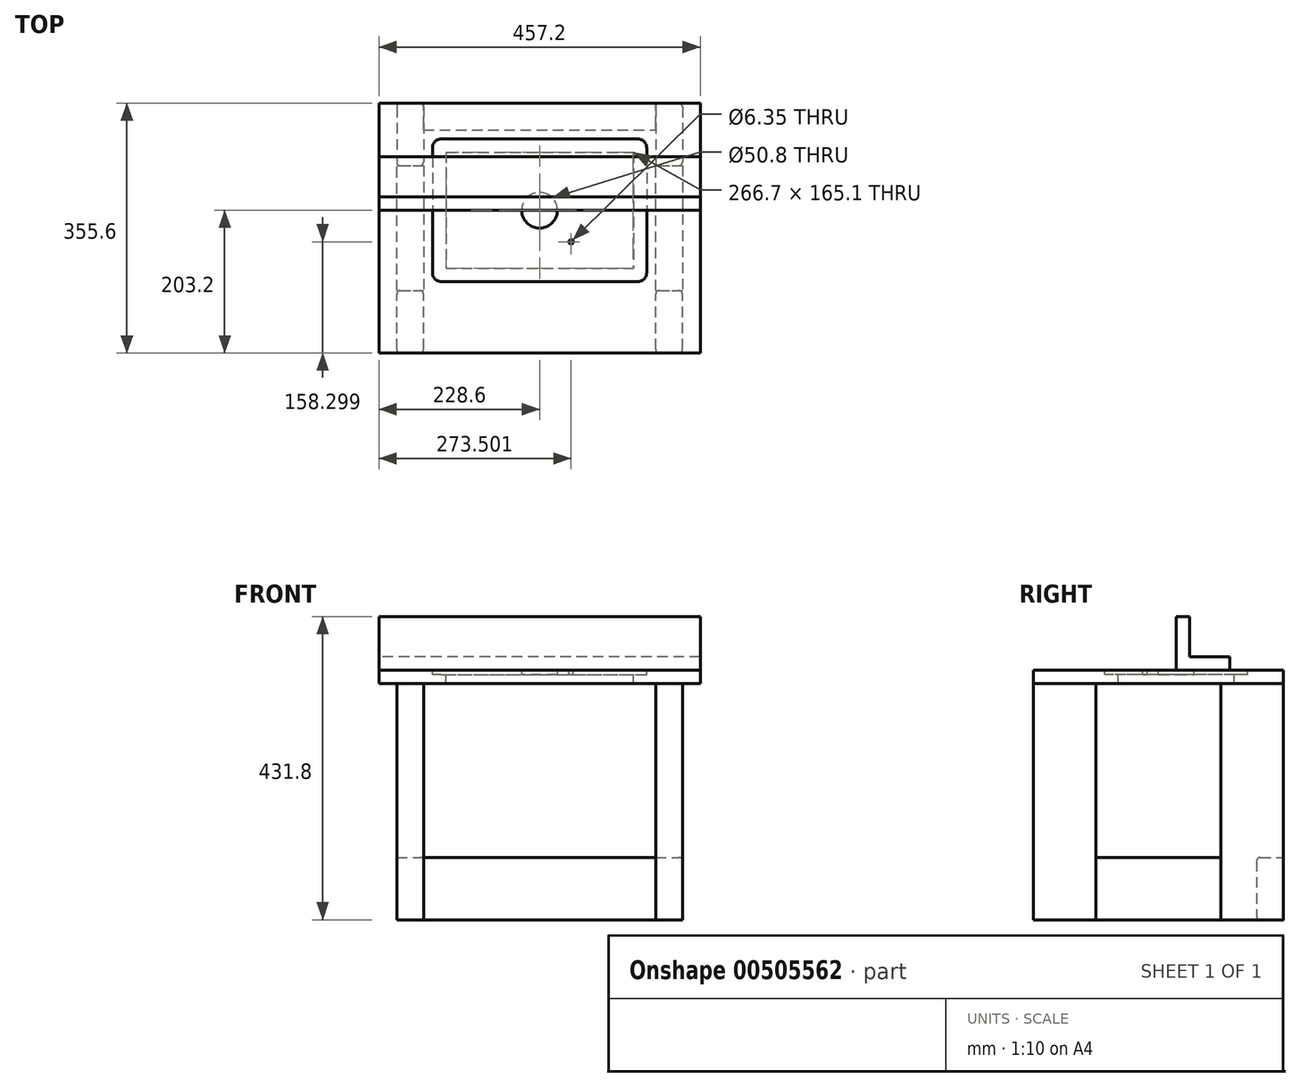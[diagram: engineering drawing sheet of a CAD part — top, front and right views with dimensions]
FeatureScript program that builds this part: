
annotation { "Feature Type Name" : "Feature", "Feature Type Description" : "" }
export const myFeature = defineFeature(function(context is Context, id is Id, definition is map)
    precondition{}
    {
        {
            var Q0;
            Q0=qCreatedBy(makeId("Top.planeOp"),FACE);
            var sketch = newSketch(context, id + "F0", { "sketchPlane" : qUnion([Q0])});
            skLineSegment(sketch, "E0.bottom", {"start": v(228.6, -177.8) * mm, "end": v(-228.6, -177.8) * mm});
            skLineSegment(sketch, "E0.top", {"start": v(228.6, 177.8) * mm, "end": v(-228.6, 177.8) * mm});
            skLineSegment(sketch, "E0.left", {"start": v(228.6, -177.8) * mm, "end": v(228.6, 177.8) * mm});
            skLineSegment(sketch, "E0.right", {"start": v(-228.6, -177.8) * mm, "end": v(-228.6, 177.8) * mm});
            skPoint(sketch, "E0.middle", {"position": v(0, 0) * mm});
            skLineSegment(sketch, "E1.bottom", {"start": v(-152.4, 127) * mm, "end": v(152.4, 127) * mm});
            skLineSegment(sketch, "E1.top", {"start": v(-152.4, -76.2) * mm, "end": v(152.4, -76.2) * mm});
            skLineSegment(sketch, "E1.left", {"start": v(-152.4, 127) * mm, "end": v(-152.4, -76.2) * mm});
            skLineSegment(sketch, "E1.right", {"start": v(152.4, 127) * mm, "end": v(152.4, -76.2) * mm});
            skLineSegment(sketch, "E2", {"start": v(0, 177.8) * mm, "end": v(0, -177.8) * mm, "construction": true});
            skLineSegment(sketch, "E3.0", {"start": v(-133.35, 107.95) * mm, "end": v(-133.35, -57.15) * mm});
            skLineSegment(sketch, "E3.1", {"start": v(-133.35, 107.95) * mm, "end": v(133.35, 107.95) * mm});
            skLineSegment(sketch, "E3.2", {"start": v(133.35, 107.95) * mm, "end": v(133.35, -57.15) * mm});
            skLineSegment(sketch, "E3.3", {"start": v(-133.35, -57.15) * mm, "end": v(133.35, -57.15) * mm});
            skSolve(sketch);
        }
        {
            var Q0;
            Q0=makeQuery(id+"F0.imprint","IMPRINT",FACE,{"disambiguationData":[TD([[makeQuery(id+"F0.imprint","IMPRINT",EDGE,{"derivedFrom":sQuery(id+"F0.wireOp",EDGE,"E0.bottom")}),-1.0]])]});
            var Q1;
            Q1=makeQuery(id+"F0.imprint","IMPRINT",FACE,{"disambiguationData":[TD([[makeQuery(id+"F0.imprint","IMPRINT",EDGE,{"derivedFrom":sQuery(id+"F0.wireOp",EDGE,"E1.bottom")}),-1.0]])]});
            extrude(context, id + "F1", {"entities" : qUnion([Q0, Q1]), "oppositeDirection" : true, "depth" : 19.05 * mm});
        }
        {
            var Q0;
            Q0=makeQuery(id+"F0.imprint","IMPRINT",FACE,{"disambiguationData":[TD([[makeQuery(id+"F0.imprint","IMPRINT",EDGE,{"derivedFrom":sQuery(id+"F0.wireOp",EDGE,"E1.bottom")}),-1.0]])]});
            extrude(context, id + "F2", {"entities" : qUnion([Q0]), "operationType" : NewBodyOperationType.REMOVE, "oppositeDirection" : true, "depth" : 6.35 * mm});
        }
        {
            var Q0;
            Q0=makeQuery(id+"F1.opExtrude","SWEPT_BODY",BODY,{"disambiguationData":[OSD([sQuery(id+"F0.wireOp",EDGE,"E0.bottom"),sQuery(id+"F0.wireOp",EDGE,"E0.top"),sQuery(id+"F0.wireOp",EDGE,"E0.left"),sQuery(id+"F0.wireOp",EDGE,"E0.right"),sQuery(id+"F0.wireOp",EDGE,"E3.0"),sQuery(id+"F0.wireOp",EDGE,"E3.1"),sQuery(id+"F0.wireOp",EDGE,"E3.2"),sQuery(id+"F0.wireOp",EDGE,"E3.3")])]});
            transform(context, id + "F3", {"entities" : qUnion([Q0]), "transformType" : TransformType.TRANSLATION_3D, "dx" : 0 * mm, "dy" : 0 * mm, "dz" : 355.6 * mm, "makeCopy" : false});
        }
        {
            var Q0;
            Q0=makeQuery(id+"F1.opExtrude","SWEPT_FACE",FACE,{"disambiguationData":[OSD([sQuery(id+"F0.wireOp",EDGE,"E0.left")])]});
            var sketch = newSketch(context, id + "F4", { "sketchPlane" : qUnion([Q0])});
            skLineSegment(sketch, "E4.bottom", {"start": v(-177.8, 336.55) * mm, "end": v(-88.9, 336.55) * mm});
            skLineSegment(sketch, "E4.top", {"start": v(-177.8, 0) * mm, "end": v(-88.9, 0) * mm});
            skLineSegment(sketch, "E4.left", {"start": v(-177.8, 336.55) * mm, "end": v(-177.8, 0) * mm});
            skLineSegment(sketch, "E4.right", {"start": v(-88.9, 336.55) * mm, "end": v(-88.9, 0) * mm});
            skLineSegment(sketch, "E5.bottom", {"start": v(177.8, 336.55) * mm, "end": v(88.9, 336.55) * mm});
            skLineSegment(sketch, "E5.top", {"start": v(177.8, 0) * mm, "end": v(88.9, 0) * mm});
            skLineSegment(sketch, "E5.left", {"start": v(177.8, 336.55) * mm, "end": v(177.8, 0) * mm});
            skLineSegment(sketch, "E5.right", {"start": v(88.9, 336.55) * mm, "end": v(88.9, 0) * mm});
            skLineSegment(sketch, "E6.bottom", {"start": v(88.9, 0) * mm, "end": v(-88.9, 0) * mm});
            skLineSegment(sketch, "E6.top", {"start": v(88.9, 88.9) * mm, "end": v(-88.9, 88.9) * mm});
            skLineSegment(sketch, "E6.left", {"start": v(88.9, 0) * mm, "end": v(88.9, 88.9) * mm});
            skLineSegment(sketch, "E6.right", {"start": v(-88.9, 0) * mm, "end": v(-88.9, 88.9) * mm});
            skSolve(sketch);
        }
        {
            var Q0;
            Q0=makeQuery(id+"F4.imprint","IMPRINT",FACE,{"disambiguationData":[TD([[makeQuery(id+"F4.imprint","IMPRINT",EDGE,{"derivedFrom":sQuery(id+"F4.wireOp",EDGE,"E4.bottom")}),-1.0]])]});
            var Q1;
            Q1=makeQuery(id+"F4.imprint","IMPRINT",FACE,{"disambiguationData":[TD([[makeQuery(id+"F4.imprint","IMPRINT",EDGE,{"derivedFrom":sQuery(id+"F4.wireOp",EDGE,"E5.bottom")}),-1.0]])]});
            extrude(context, id + "F5", {"entities" : qUnion([Q0, Q1]), "oppositeDirection" : true, "depth" : 38.1 * mm});
        }
        {
            var Q0;
            Q0=makeQuery(id+"F4.imprint","IMPRINT",FACE,{"disambiguationData":[TD([[makeQuery(id+"F4.imprint","IMPRINT",EDGE,{"derivedFrom":sQuery(id+"F4.wireOp",EDGE,"E6.bottom")}),-1.0]])]});
            var Q1;
            Q1=makeQuery(id+"F5.opExtrude","CAP_FACE",FACE,{"disambiguationData":[OSD([sQuery(id+"F4.wireOp",EDGE,"E4.bottom"),sQuery(id+"F4.wireOp",EDGE,"E4.top"),sQuery(id+"F4.wireOp",EDGE,"E4.left"),sQuery(id+"F4.wireOp",EDGE,"E4.right"),sQuery(id+"F4.wireOp",EDGE,"E6.right")])],"isStart":false});
            extrude(context, id + "F6", {"entities" : qUnion([Q0]), "endBound" : BoundingType.UP_TO_SURFACE, "oppositeDirection" : true, "endBoundEntityFace" : qUnion([Q1]), "depth" : 25.4 * mm});
        }
        {
            var Q0;
            Q0=makeQuery(id+"F5.opExtrude","SWEPT_BODY",BODY,{"disambiguationData":[OSD([sQuery(id+"F4.wireOp",EDGE,"E4.bottom"),sQuery(id+"F4.wireOp",EDGE,"E4.top"),sQuery(id+"F4.wireOp",EDGE,"E4.left"),sQuery(id+"F4.wireOp",EDGE,"E4.right"),sQuery(id+"F4.wireOp",EDGE,"E6.right")])]});
            var Q1;
            Q1=makeQuery(id+"F5.opExtrude","SWEPT_BODY",BODY,{"disambiguationData":[OSD([sQuery(id+"F4.wireOp",EDGE,"E5.bottom"),sQuery(id+"F4.wireOp",EDGE,"E5.top"),sQuery(id+"F4.wireOp",EDGE,"E5.left"),sQuery(id+"F4.wireOp",EDGE,"E5.right"),sQuery(id+"F4.wireOp",EDGE,"E6.left")])]});
            var Q2;
            Q2=makeQuery(id+"F6.opExtrude","SWEPT_BODY",BODY,{"disambiguationData":[OSD([sQuery(id+"F4.wireOp",EDGE,"E6.bottom"),sQuery(id+"F4.wireOp",EDGE,"E6.top"),sQuery(id+"F4.wireOp",EDGE,"E6.left"),sQuery(id+"F4.wireOp",EDGE,"E6.right")])]});
            var Q3;
            Q3=makeQuery(id+"F1.opExtrude","CAP_EDGE",EDGE,{"disambiguationData":[OSD([sQuery(id+"F0.wireOp",EDGE,"E0.bottom")])],"isStart":false});
            var Q4;
            Q4=makeQuery(id+"F1.opExtrude","CAP_EDGE",EDGE,{"disambiguationData":[OSD([sQuery(id+"F0.wireOp",EDGE,"E0.bottom")])],"isStart":false});
            transform(context, id + "F7", {"entities" : qUnion([Q0, Q1, Q2]), "transformType" : TransformType.TRANSLATION_DISTANCE, "transformDirection" : qUnion([Q4]), "distance" : 393.7 * mm, "makeCopy" : true});
        }
        {
            var Q0;
            Q0=makeQuery(id+"F5.opExtrude","SWEPT_BODY",BODY,{"disambiguationData":[OSD([sQuery(id+"F4.wireOp",EDGE,"E5.bottom"),sQuery(id+"F4.wireOp",EDGE,"E5.top"),sQuery(id+"F4.wireOp",EDGE,"E5.left"),sQuery(id+"F4.wireOp",EDGE,"E5.right"),sQuery(id+"F4.wireOp",EDGE,"E6.left")])]});
            var Q1;
            Q1=makeQuery(id+"F5.opExtrude","SWEPT_BODY",BODY,{"disambiguationData":[OSD([sQuery(id+"F4.wireOp",EDGE,"E4.bottom"),sQuery(id+"F4.wireOp",EDGE,"E4.top"),sQuery(id+"F4.wireOp",EDGE,"E4.left"),sQuery(id+"F4.wireOp",EDGE,"E4.right"),sQuery(id+"F4.wireOp",EDGE,"E6.right")])]});
            var Q2;
            Q2=makeQuery(id+"F6.opExtrude","SWEPT_BODY",BODY,{"disambiguationData":[OSD([sQuery(id+"F4.wireOp",EDGE,"E6.bottom"),sQuery(id+"F4.wireOp",EDGE,"E6.top"),sQuery(id+"F4.wireOp",EDGE,"E6.left"),sQuery(id+"F4.wireOp",EDGE,"E6.right")])]});
            var Q3;
            Q3=makeQuery(id+"F1.opExtrude","CAP_EDGE",EDGE,{"disambiguationData":[OSD([sQuery(id+"F0.wireOp",EDGE,"E0.bottom")])],"isStart":false});
            transform(context, id + "F8", {"entities" : qUnion([Q0, Q1, Q2]), "transformType" : TransformType.TRANSLATION_DISTANCE, "transformDirection" : qUnion([Q3]), "distance" : 25.4 * mm, "makeCopy" : false});
        }
        {
            var Q0;
            Q0=makeQuery(id+"F1.opExtrude","SWEPT_FACE",FACE,{"disambiguationData":[OSD([sQuery(id+"F0.wireOp",EDGE,"E0.top")])]});
            var sketch = newSketch(context, id + "F9", { "sketchPlane" : qUnion([Q0])});
            skLineSegment(sketch, "E7.0", {"start": v(165.1, 336.55) * mm, "end": v(165.1, 0) * mm});
            skLineSegment(sketch, "E8.0", {"start": v(-165.1, 336.55) * mm, "end": v(-165.1, 0) * mm});
            skLineSegment(sketch, "E9.bottom", {"start": v(165.1, 0) * mm, "end": v(-165.1, 0) * mm});
            skLineSegment(sketch, "E9.top", {"start": v(165.1, 88.9) * mm, "end": v(-165.1, 88.9) * mm});
            skLineSegment(sketch, "E9.left", {"start": v(165.1, 0) * mm, "end": v(165.1, 88.9) * mm});
            skLineSegment(sketch, "E9.right", {"start": v(-165.1, 0) * mm, "end": v(-165.1, 88.9) * mm});
            skSolve(sketch);
        }
        {
            var Q0;
            Q0=makeQuery(id+"F9.imprint","IMPRINT",FACE,{"disambiguationData":[TD([[makeQuery(id+"F9.imprint","IMPRINT",EDGE,{"derivedFrom":sQuery(id+"F9.wireOp",EDGE,"E9.bottom")}),-1.0]])]});
            extrude(context, id + "F10", {"entities" : qUnion([Q0]), "oppositeDirection" : true, "depth" : 38.1 * mm, "offsetDistance" : 25.4 * mm});
        }
        {
            var Q0;
            Q0=makeQuery(id+"F5.opExtrude","CAP_EDGE",EDGE,{"disambiguationData":[OSD([sQuery(id+"F4.wireOp",EDGE,"E4.left")])],"isStart":true});
            var Q1;
            Q1=makeQuery(id+"F5.opExtrude","CAP_EDGE",EDGE,{"disambiguationData":[OSD([sQuery(id+"F4.wireOp",EDGE,"E4.left")])],"isStart":false});
            var Q2;
            Q2=makeQuery(id+"F5.opExtrude","CAP_EDGE",EDGE,{"disambiguationData":[OSD([sQuery(id+"F4.wireOp",EDGE,"E4.right"),sQuery(id+"F4.wireOp",EDGE,"E6.right")])],"isStart":true});
            var Q3;
            Q3=makeQuery(id+"F6.opExtrude","TWEAK_EDGE",EDGE,{"derivedFrom":[makeQuery(id+"F4.imprint","IMPRINT",EDGE,{"derivedFrom":sQuery(id+"F4.wireOp",EDGE,"E6.top")}),makeQuery(id+"F5.opExtrude","CAP_FACE",FACE,{"disambiguationData":[OSD([sQuery(id+"F4.wireOp",EDGE,"E4.bottom"),sQuery(id+"F4.wireOp",EDGE,"E4.top"),sQuery(id+"F4.wireOp",EDGE,"E4.left"),sQuery(id+"F4.wireOp",EDGE,"E4.right"),sQuery(id+"F4.wireOp",EDGE,"E6.right")])],"isStart":false})]});
            var Q4;
            Q4=makeQuery(id+"F6.opExtrude","CAP_EDGE",EDGE,{"disambiguationData":[OSD([sQuery(id+"F4.wireOp",EDGE,"E6.top")])],"isStart":true});
            var Q5;
            Q5=makeQuery(id+"F6.opExtrude","CAP_EDGE",EDGE,{"disambiguationData":[OSD([sQuery(id+"F4.wireOp",EDGE,"E6.bottom")])],"isStart":true});
            var Q6;
            Q6=makeQuery(id+"F5.opExtrude","CAP_EDGE",EDGE,{"disambiguationData":[OSD([sQuery(id+"F4.wireOp",EDGE,"E5.right"),sQuery(id+"F4.wireOp",EDGE,"E6.left")])],"isStart":true});
            var Q7;
            Q7=makeQuery(id+"F5.opExtrude","CAP_EDGE",EDGE,{"disambiguationData":[OSD([sQuery(id+"F4.wireOp",EDGE,"E5.right"),sQuery(id+"F4.wireOp",EDGE,"E6.left")])],"isStart":false});
            var Q8;
            Q8=makeQuery(id+"F5.opExtrude","CAP_EDGE",EDGE,{"disambiguationData":[OSD([sQuery(id+"F4.wireOp",EDGE,"E5.left")])],"isStart":true});
            var Q9;
            Q9=makeQuery(id+"F5.opExtrude","CAP_EDGE",EDGE,{"disambiguationData":[OSD([sQuery(id+"F4.wireOp",EDGE,"E4.right"),sQuery(id+"F4.wireOp",EDGE,"E6.right")])],"isStart":false});
            var Q10;
            Q10=makeQuery(id+"F6.opExtrude","TWEAK_EDGE",EDGE,{"derivedFrom":[makeQuery(id+"F4.imprint","IMPRINT",EDGE,{"derivedFrom":sQuery(id+"F4.wireOp",EDGE,"E6.bottom")}),makeQuery(id+"F5.opExtrude","CAP_FACE",FACE,{"disambiguationData":[OSD([sQuery(id+"F4.wireOp",EDGE,"E4.bottom"),sQuery(id+"F4.wireOp",EDGE,"E4.top"),sQuery(id+"F4.wireOp",EDGE,"E4.left"),sQuery(id+"F4.wireOp",EDGE,"E4.right"),sQuery(id+"F4.wireOp",EDGE,"E6.right")])],"isStart":false})]});
            var Q11;
            Q11=makeQuery(id+"F5.opExtrude","CAP_EDGE",EDGE,{"disambiguationData":[OSD([sQuery(id+"F4.wireOp",EDGE,"E5.left")])],"isStart":false});
            var Q12;
            Q12=makeQuery(id+"F7.opPattern","COPY",EDGE,{"derivedFrom":makeQuery(id+"F6.opExtrude","TWEAK_EDGE",EDGE,{"derivedFrom":[makeQuery(id+"F4.imprint","IMPRINT",EDGE,{"derivedFrom":sQuery(id+"F4.wireOp",EDGE,"E6.top")}),makeQuery(id+"F5.opExtrude","CAP_FACE",FACE,{"disambiguationData":[OSD([sQuery(id+"F4.wireOp",EDGE,"E4.bottom"),sQuery(id+"F4.wireOp",EDGE,"E4.top"),sQuery(id+"F4.wireOp",EDGE,"E4.left"),sQuery(id+"F4.wireOp",EDGE,"E4.right"),sQuery(id+"F4.wireOp",EDGE,"E6.right")])],"isStart":false})]}),"instanceName":"1"});
            var Q13;
            Q13=makeQuery(id+"F7.opPattern","COPY",EDGE,{"derivedFrom":makeQuery(id+"F6.opExtrude","CAP_EDGE",EDGE,{"disambiguationData":[OSD([sQuery(id+"F4.wireOp",EDGE,"E6.top")])],"isStart":true}),"instanceName":"1"});
            var Q14;
            Q14=makeQuery(id+"F7.opPattern","COPY",EDGE,{"derivedFrom":makeQuery(id+"F6.opExtrude","CAP_EDGE",EDGE,{"disambiguationData":[OSD([sQuery(id+"F4.wireOp",EDGE,"E6.bottom")])],"isStart":true}),"instanceName":"1"});
            var Q15;
            Q15=makeQuery(id+"F7.opPattern","COPY",EDGE,{"derivedFrom":makeQuery(id+"F5.opExtrude","CAP_EDGE",EDGE,{"disambiguationData":[OSD([sQuery(id+"F4.wireOp",EDGE,"E4.right"),sQuery(id+"F4.wireOp",EDGE,"E6.right")])],"isStart":true}),"instanceName":"1"});
            var Q16;
            Q16=makeQuery(id+"F7.opPattern","COPY",EDGE,{"derivedFrom":makeQuery(id+"F5.opExtrude","CAP_EDGE",EDGE,{"disambiguationData":[OSD([sQuery(id+"F4.wireOp",EDGE,"E4.left")])],"isStart":true}),"instanceName":"1"});
            var Q17;
            Q17=makeQuery(id+"F7.opPattern","COPY",EDGE,{"derivedFrom":makeQuery(id+"F5.opExtrude","CAP_EDGE",EDGE,{"disambiguationData":[OSD([sQuery(id+"F4.wireOp",EDGE,"E4.left")])],"isStart":false}),"instanceName":"1"});
            var Q18;
            Q18=makeQuery(id+"F7.opPattern","COPY",EDGE,{"derivedFrom":makeQuery(id+"F5.opExtrude","CAP_EDGE",EDGE,{"disambiguationData":[OSD([sQuery(id+"F4.wireOp",EDGE,"E5.right"),sQuery(id+"F4.wireOp",EDGE,"E6.left")])],"isStart":false}),"instanceName":"1"});
            var Q19;
            Q19=makeQuery(id+"F7.opPattern","COPY",EDGE,{"derivedFrom":makeQuery(id+"F5.opExtrude","CAP_EDGE",EDGE,{"disambiguationData":[OSD([sQuery(id+"F4.wireOp",EDGE,"E5.right"),sQuery(id+"F4.wireOp",EDGE,"E6.left")])],"isStart":true}),"instanceName":"1"});
            var Q20;
            Q20=makeQuery(id+"F7.opPattern","COPY",EDGE,{"derivedFrom":makeQuery(id+"F5.opExtrude","CAP_EDGE",EDGE,{"disambiguationData":[OSD([sQuery(id+"F4.wireOp",EDGE,"E5.left")])],"isStart":true}),"instanceName":"1"});
            var Q21;
            Q21=makeQuery(id+"F7.opPattern","COPY",EDGE,{"derivedFrom":makeQuery(id+"F5.opExtrude","CAP_EDGE",EDGE,{"disambiguationData":[OSD([sQuery(id+"F4.wireOp",EDGE,"E4.right"),sQuery(id+"F4.wireOp",EDGE,"E6.right")])],"isStart":false}),"instanceName":"1"});
            var Q22;
            Q22=makeQuery(id+"F7.opPattern","COPY",EDGE,{"derivedFrom":makeQuery(id+"F6.opExtrude","TWEAK_EDGE",EDGE,{"derivedFrom":[makeQuery(id+"F4.imprint","IMPRINT",EDGE,{"derivedFrom":sQuery(id+"F4.wireOp",EDGE,"E6.bottom")}),makeQuery(id+"F5.opExtrude","CAP_FACE",FACE,{"disambiguationData":[OSD([sQuery(id+"F4.wireOp",EDGE,"E4.bottom"),sQuery(id+"F4.wireOp",EDGE,"E4.top"),sQuery(id+"F4.wireOp",EDGE,"E4.left"),sQuery(id+"F4.wireOp",EDGE,"E4.right"),sQuery(id+"F4.wireOp",EDGE,"E6.right")])],"isStart":false})]}),"instanceName":"1"});
            var Q23;
            Q23=makeQuery(id+"F7.opPattern","COPY",EDGE,{"derivedFrom":makeQuery(id+"F5.opExtrude","CAP_EDGE",EDGE,{"disambiguationData":[OSD([sQuery(id+"F4.wireOp",EDGE,"E5.left")])],"isStart":false}),"instanceName":"1"});
            var Q24;
            Q24=makeQuery(id+"F10.opExtrude","CAP_EDGE",EDGE,{"disambiguationData":[OSD([sQuery(id+"F9.wireOp",EDGE,"E9.top")])],"isStart":false});
            var Q25;
            Q25=makeQuery(id+"F10.opExtrude","CAP_EDGE",EDGE,{"disambiguationData":[OSD([sQuery(id+"F9.wireOp",EDGE,"E9.bottom")])],"isStart":true});
            var Q26;
            Q26=makeQuery(id+"F10.opExtrude","CAP_EDGE",EDGE,{"disambiguationData":[OSD([sQuery(id+"F9.wireOp",EDGE,"E9.bottom")])],"isStart":false});
            fillet(context, id + "F11", {"entities" : qUnion([Q0, Q1, Q2, Q3, Q4, Q5, Q6, Q7, Q8, Q9, Q10, Q11, Q12, Q13, Q14, Q15, Q16, Q17, Q18, Q19, Q20, Q21, Q22, Q23, Q24, Q25, Q26]), "radius" : 5.08 * mm, "tangentPropagation" : true, "allowEdgeOverflow" : false});
        }
        {
            var Q0;
            Q0=makeQuery(id+"F2.boolean.opBoolean","COPY",EDGE,{"derivedFrom":makeQuery(id+"F2.opExtrude","SWEPT_EDGE",EDGE,{"disambiguationData":[OSD([sQuery(id+"F0.wireOp",EDGE,"E1.bottom"),sQuery(id+"F0.wireOp",EDGE,"E1.left")])]})});
            var Q1;
            Q1=makeQuery(id+"F2.boolean.opBoolean","COPY",EDGE,{"derivedFrom":makeQuery(id+"F2.opExtrude","SWEPT_EDGE",EDGE,{"disambiguationData":[OSD([sQuery(id+"F0.wireOp",EDGE,"E1.bottom"),sQuery(id+"F0.wireOp",EDGE,"E1.right")])]})});
            var Q2;
            Q2=makeQuery(id+"F2.boolean.opBoolean","COPY",EDGE,{"derivedFrom":makeQuery(id+"F2.opExtrude","SWEPT_EDGE",EDGE,{"disambiguationData":[OSD([sQuery(id+"F0.wireOp",EDGE,"E1.top"),sQuery(id+"F0.wireOp",EDGE,"E1.right")])]})});
            var Q3;
            Q3=makeQuery(id+"F2.boolean.opBoolean","COPY",EDGE,{"derivedFrom":makeQuery(id+"F2.opExtrude","SWEPT_EDGE",EDGE,{"disambiguationData":[OSD([sQuery(id+"F0.wireOp",EDGE,"E1.top"),sQuery(id+"F0.wireOp",EDGE,"E1.left")])]})});
            fillet(context, id + "F12", {"entities" : qUnion([Q0, Q1, Q2, Q3]), "radius" : 12.7 * mm, "tangentPropagation" : true, "allowEdgeOverflow" : false});
        }
        {
            var Q0;
            Q0=makeQuery(id+"F1.opExtrude","CAP_FACE",FACE,{"disambiguationData":[OSD([sQuery(id+"F0.wireOp",EDGE,"E0.bottom"),sQuery(id+"F0.wireOp",EDGE,"E0.top"),sQuery(id+"F0.wireOp",EDGE,"E0.left"),sQuery(id+"F0.wireOp",EDGE,"E0.right"),sQuery(id+"F0.wireOp",EDGE,"E3.0"),sQuery(id+"F0.wireOp",EDGE,"E3.1"),sQuery(id+"F0.wireOp",EDGE,"E3.2"),sQuery(id+"F0.wireOp",EDGE,"E3.3")])],"isStart":true});
            var sketch = newSketch(context, id + "F13", { "sketchPlane" : qUnion([Q0])});
            skLineSegment(sketch, "E10.0.0", {"start": v(139.7, 127) * mm, "end": v(-139.7, 127) * mm});
            skArc(sketch, "E10.0.1", {"start": v(-139.7, 127) * mm, "mid": v(-148.68, 123.28) * mm, "end": v(-152.4, 114.3) * mm});
            skLineSegment(sketch, "E10.0.2", {"start": v(-152.4, 114.3) * mm, "end": v(-152.4, -63.5) * mm});
            skArc(sketch, "E10.0.3", {"start": v(-152.4, -63.5) * mm, "mid": v(-148.68, -72.48) * mm, "end": v(-139.7, -76.2) * mm});
            skLineSegment(sketch, "E10.0.4", {"start": v(-139.7, -76.2) * mm, "end": v(139.7, -76.2) * mm});
            skArc(sketch, "E10.0.5", {"start": v(139.7, -76.2) * mm, "mid": v(148.68, -72.48) * mm, "end": v(152.4, -63.5) * mm});
            skLineSegment(sketch, "E10.0.6", {"start": v(152.4, -63.5) * mm, "end": v(152.4, 114.3) * mm});
            skArc(sketch, "E10.0.7", {"start": v(152.4, 114.3) * mm, "mid": v(148.68, 123.28) * mm, "end": v(139.7, 127) * mm});
            skLineSegment(sketch, "E11", {"start": v(0, 127) * mm, "end": v(0, -76.2) * mm, "construction": true});
            skLineSegment(sketch, "E12", {"start": v(152.4, 25.4) * mm, "end": v(-152.4, 25.4) * mm, "construction": true});
            skCircle(sketch, "E13", {"center": v(0, 25.4) * mm, "radius": 76.2 * mm, "construction": true});
            skCircle(sketch, "E14", {"center": v(0, 25.4) * mm, "radius": 25.4 * mm});
            skLineSegment(sketch, "E15", {"start": v(0, 25.4) * mm, "end": v(44.9, -19.5) * mm, "construction": true});
            skCircle(sketch, "E16", {"center": v(44.9, -19.5) * mm, "radius": 3.18 * mm});
            skSolve(sketch);
        }
        {
            var Q0;
            Q0 = qSketchRegion(id + "F13", true);
            extrude(context, id + "F14", {"entities" : qUnion([Q0]), "oppositeDirection" : true, "depth" : 6.35 * mm});
        }
        {
            var Q0;
            Q0=qCreatedBy(makeId("Right.planeOp"),FACE);
            var sketch = newSketch(context, id + "F15", { "sketchPlane" : qUnion([Q0])});
            skLineSegment(sketch, "E17.bottom", {"start": v(25.4, 431.8) * mm, "end": v(101.6, 431.8) * mm, "construction": true});
            skLineSegment(sketch, "E17.top", {"start": v(25.4, 355.6) * mm, "end": v(101.6, 355.6) * mm});
            skLineSegment(sketch, "E17.left", {"start": v(25.4, 431.8) * mm, "end": v(25.4, 355.6) * mm});
            skLineSegment(sketch, "E17.right", {"start": v(101.6, 431.8) * mm, "end": v(101.6, 355.6) * mm, "construction": true});
            skLineSegment(sketch, "E18.0", {"start": v(0, 355.6) * mm, "end": v(50.8, 355.6) * mm});
            skLineSegment(sketch, "E19.bottom", {"start": v(25.4, 431.8) * mm, "end": v(44.45, 431.8) * mm});
            skLineSegment(sketch, "E19.top", {"start": v(25.4, 355.6) * mm, "end": v(44.45, 355.6) * mm});
            skLineSegment(sketch, "E19.right", {"start": v(44.45, 431.8) * mm, "end": v(44.45, 355.6) * mm});
            skLineSegment(sketch, "E20.bottom", {"start": v(101.6, 355.6) * mm, "end": v(25.4, 355.6) * mm});
            skLineSegment(sketch, "E20.top", {"start": v(101.6, 374.65) * mm, "end": v(25.4, 374.65) * mm});
            skLineSegment(sketch, "E20.left", {"start": v(101.6, 355.6) * mm, "end": v(101.6, 374.65) * mm});
            skLineSegment(sketch, "E20.right", {"start": v(25.4, 355.6) * mm, "end": v(25.4, 374.65) * mm});
            skSolve(sketch);
        }
        {
            var Q0;
            Q0 = qSketchRegion(id + "F15", true);
            extrude(context, id + "F16", {"entities" : qUnion([Q0]), "endBound" : BoundingType.SYMMETRIC, "depth" : 457.2 * mm, "offsetDistance" : 25.4 * mm});
        }
    });
